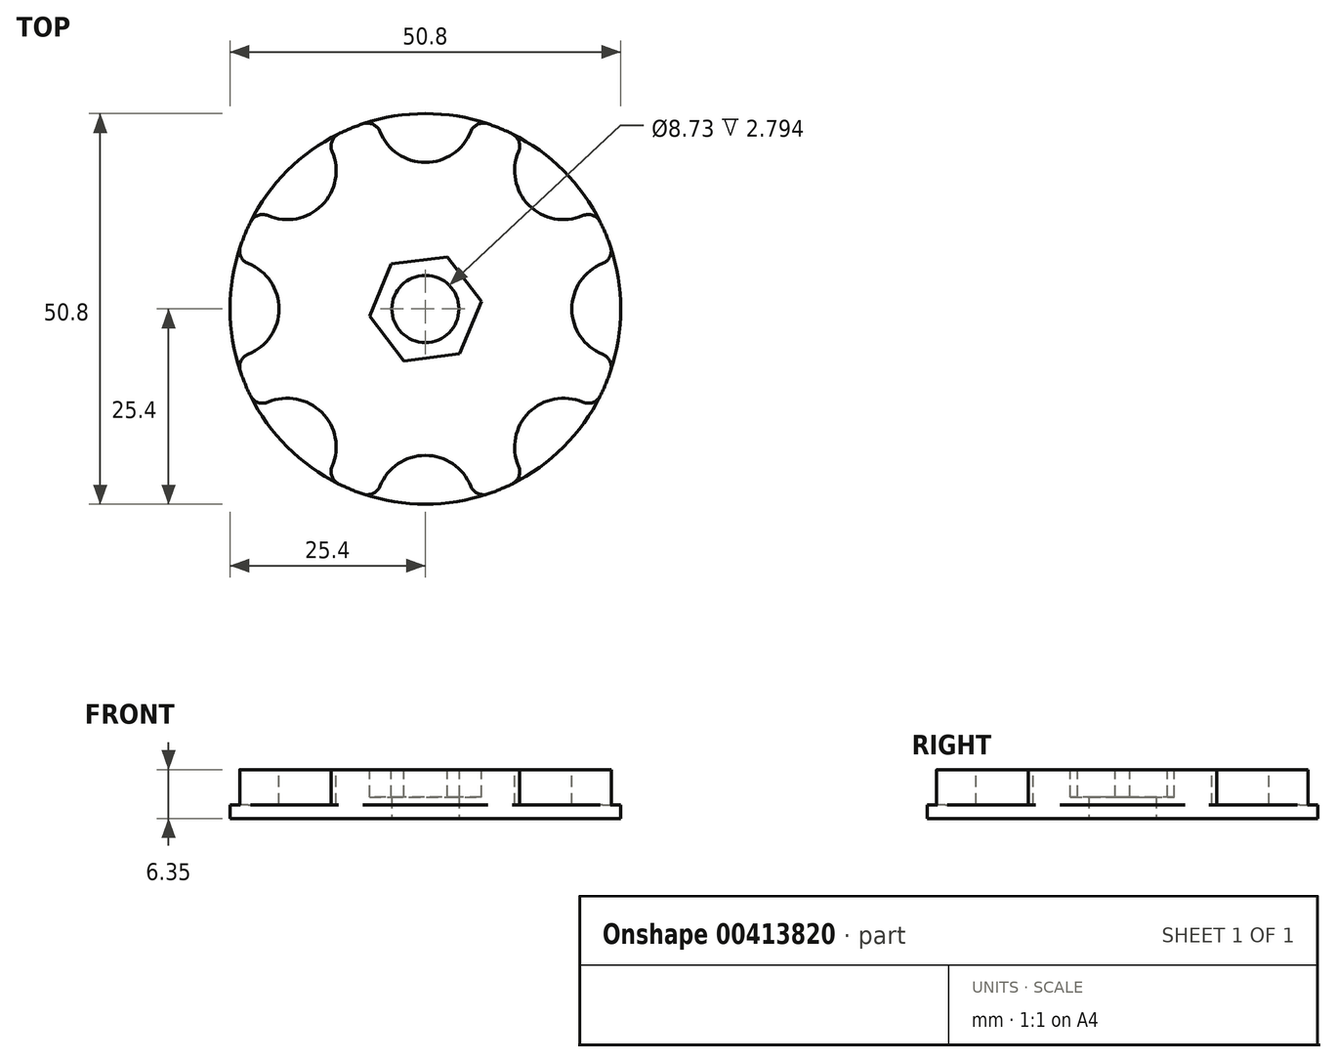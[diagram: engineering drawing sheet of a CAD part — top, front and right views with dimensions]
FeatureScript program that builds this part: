
annotation { "Feature Type Name" : "Feature", "Feature Type Description" : "" }
export const myFeature = defineFeature(function(context is Context, id is Id, definition is map)
    precondition{}
    {
        {
            var Q0;
            Q0=qCreatedBy(makeId("Top.planeOp"),FACE);
            var sketch = newSketch(context, id + "F0", { "sketchPlane" : qUnion([Q0])});
            skCircle(sketch, "E0", {"center": v(0, 0) * mm, "radius": 4.37 * mm});
            skCircle(sketch, "E1", {"center": v(0, 0) * mm, "radius": 25.4 * mm});
            skSolve(sketch);
        }
        {
            var Q0;
            Q0=makeQuery(id+"F0.imprint","IMPRINT",FACE,{"disambiguationData":[TD([[makeQuery(id+"F0.imprint","IMPRINT",EDGE,{"derivedFrom":sQuery(id+"F0.wireOp",EDGE,"E0")}),-1.0]])]});
            extrude(context, id + "F1", {"entities" : qUnion([Q0]), "depth" : 6.35 * mm});
        }
        {
            var Q0;
            Q0=makeQuery(id+"F1.opExtrude","CAP_FACE",FACE,{"disambiguationData":[OSD([sQuery(id+"F0.wireOp",EDGE,"E0"),sQuery(id+"F0.wireOp",EDGE,"E1")])],"isStart":false});
            var sketch = newSketch(context, id + "F2", { "sketchPlane" : qUnion([Q0])});
            skCircle(sketch, "E2.cCircle", {"center": v(0, 0) * mm, "radius": 6.35 * mm, "construction": true});
            skLineSegment(sketch, "E2.0", {"start": v(-2.82, -6.77) * mm, "end": v(-7.27, -0.94) * mm});
            skLineSegment(sketch, "E2.1", {"start": v(-7.27, -0.94) * mm, "end": v(-4.45, 5.83) * mm});
            skLineSegment(sketch, "E2.2", {"start": v(-4.45, 5.83) * mm, "end": v(2.82, 6.77) * mm});
            skLineSegment(sketch, "E2.3", {"start": v(2.82, 6.77) * mm, "end": v(7.27, 0.94) * mm});
            skLineSegment(sketch, "E2.4", {"start": v(7.27, 0.94) * mm, "end": v(4.45, -5.83) * mm});
            skLineSegment(sketch, "E2.5", {"start": v(4.45, -5.83) * mm, "end": v(-2.82, -6.77) * mm});
            skPoint(sketch, "E2.0.midPoint", {"position": v(-5.05, -3.85) * mm});
            skSolve(sketch);
        }
        {
            var Q0;
            Q0=makeQuery(id+"F2.imprint","IMPRINT",FACE,{"disambiguationData":[TD([[makeQuery(id+"F2.imprint","IMPRINT",EDGE,{"derivedFrom":sQuery(id+"F2.wireOp",EDGE,"E2.0")}),-1.0]])]});
            extrude(context, id + "F3", {"entities" : qUnion([Q0]), "operationType" : NewBodyOperationType.REMOVE, "oppositeDirection" : true, "depth" : 3.56 * mm});
        }
        {
            var Q0;
            Q0=makeQuery(id+"F1.opExtrude","CAP_FACE",FACE,{"disambiguationData":[OSD([sQuery(id+"F0.wireOp",EDGE,"E0"),sQuery(id+"F0.wireOp",EDGE,"E1")])],"isStart":false});
            var sketch = newSketch(context, id + "F4", { "sketchPlane" : qUnion([Q0])});
            skCircle(sketch, "E3", {"center": v(0, 25.4) * mm, "radius": 6.35 * mm});
            skCircle(sketch, "E4.1.0", {"center": v(-17.96, 17.96) * mm, "radius": 6.35 * mm});
            skCircle(sketch, "E4.2.0", {"center": v(-25.4, 0) * mm, "radius": 6.35 * mm});
            skCircle(sketch, "E4.3.0", {"center": v(-17.96, -17.96) * mm, "radius": 6.35 * mm});
            skCircle(sketch, "E4.4.0", {"center": v(0, -25.4) * mm, "radius": 6.35 * mm});
            skCircle(sketch, "E4.5.0", {"center": v(17.96, -17.96) * mm, "radius": 6.35 * mm});
            skCircle(sketch, "E4.6.0", {"center": v(25.4, 0) * mm, "radius": 6.35 * mm});
            skCircle(sketch, "E4.7.0", {"center": v(17.96, 17.96) * mm, "radius": 6.35 * mm});
            skPoint(sketch, "E4.center", {"position": v(0, 0) * mm});
            skSolve(sketch);
        }
        {
            var Q0;
            Q0 = qSketchRegion(id + "F4", true);
            extrude(context, id + "F5", {"entities" : qUnion([Q0]), "operationType" : NewBodyOperationType.REMOVE, "oppositeDirection" : true, "depth" : 4.57 * mm});
        }
        {
            var Q0;
            Q0=makeQuery(id+"F5.boolean.opBoolean","INTERSECT",EDGE,{"disambiguationData":[OD(0.0)],"derivedFrom":[makeQuery(id+"F1.opExtrude","SWEPT_FACE",FACE,{"disambiguationData":[OSD([sQuery(id+"F0.wireOp",EDGE,"E1")])]}),makeQuery(id+"F5.opExtrude","SWEPT_FACE",FACE,{"disambiguationData":[OSD([sQuery(id+"F4.wireOp",EDGE,"E4.5.0")])]})]});
            var Q1;
            Q1=makeQuery(id+"F5.boolean.opBoolean","INTERSECT",EDGE,{"disambiguationData":[OD(1.0)],"derivedFrom":[makeQuery(id+"F1.opExtrude","SWEPT_FACE",FACE,{"disambiguationData":[OSD([sQuery(id+"F0.wireOp",EDGE,"E1")])]}),makeQuery(id+"F5.opExtrude","SWEPT_FACE",FACE,{"disambiguationData":[OSD([sQuery(id+"F4.wireOp",EDGE,"E4.5.0")])]})]});
            var Q2;
            Q2=makeQuery(id+"F5.boolean.opBoolean","INTERSECT",EDGE,{"disambiguationData":[OD(0.0)],"derivedFrom":[makeQuery(id+"F1.opExtrude","SWEPT_FACE",FACE,{"disambiguationData":[OSD([sQuery(id+"F0.wireOp",EDGE,"E1")])]}),makeQuery(id+"F5.opExtrude","SWEPT_FACE",FACE,{"disambiguationData":[OSD([sQuery(id+"F4.wireOp",EDGE,"E4.6.0")])]})]});
            var Q3;
            Q3=makeQuery(id+"F5.boolean.opBoolean","INTERSECT",EDGE,{"disambiguationData":[OD(1.0)],"derivedFrom":[makeQuery(id+"F1.opExtrude","SWEPT_FACE",FACE,{"disambiguationData":[OSD([sQuery(id+"F0.wireOp",EDGE,"E1")])]}),makeQuery(id+"F5.opExtrude","SWEPT_FACE",FACE,{"disambiguationData":[OSD([sQuery(id+"F4.wireOp",EDGE,"E4.6.0")])]})]});
            var Q4;
            Q4=makeQuery(id+"F5.boolean.opBoolean","INTERSECT",EDGE,{"disambiguationData":[OD(1.0)],"derivedFrom":[makeQuery(id+"F1.opExtrude","SWEPT_FACE",FACE,{"disambiguationData":[OSD([sQuery(id+"F0.wireOp",EDGE,"E1")])]}),makeQuery(id+"F5.opExtrude","SWEPT_FACE",FACE,{"disambiguationData":[OSD([sQuery(id+"F4.wireOp",EDGE,"E4.7.0")])]})]});
            var Q5;
            Q5=makeQuery(id+"F5.boolean.opBoolean","INTERSECT",EDGE,{"disambiguationData":[OD(0.0)],"derivedFrom":[makeQuery(id+"F1.opExtrude","SWEPT_FACE",FACE,{"disambiguationData":[OSD([sQuery(id+"F0.wireOp",EDGE,"E1")])]}),makeQuery(id+"F5.opExtrude","SWEPT_FACE",FACE,{"disambiguationData":[OSD([sQuery(id+"F4.wireOp",EDGE,"E4.7.0")])]})]});
            var Q6;
            Q6=makeQuery(id+"F5.boolean.opBoolean","INTERSECT",EDGE,{"disambiguationData":[OD(0.0)],"derivedFrom":[makeQuery(id+"F1.opExtrude","SWEPT_FACE",FACE,{"disambiguationData":[OSD([sQuery(id+"F0.wireOp",EDGE,"E1")])]}),makeQuery(id+"F5.opExtrude","SWEPT_FACE",FACE,{"disambiguationData":[OSD([sQuery(id+"F4.wireOp",EDGE,"E4.4.0")])]})]});
            var Q7;
            Q7=makeQuery(id+"F5.boolean.opBoolean","INTERSECT",EDGE,{"disambiguationData":[OD(1.0)],"derivedFrom":[makeQuery(id+"F1.opExtrude","SWEPT_FACE",FACE,{"disambiguationData":[OSD([sQuery(id+"F0.wireOp",EDGE,"E1")])]}),makeQuery(id+"F5.opExtrude","SWEPT_FACE",FACE,{"disambiguationData":[OSD([sQuery(id+"F4.wireOp",EDGE,"E3")])]})]});
            var Q8;
            Q8=makeQuery(id+"F5.boolean.opBoolean","INTERSECT",EDGE,{"disambiguationData":[OD(0.0)],"derivedFrom":[makeQuery(id+"F1.opExtrude","SWEPT_FACE",FACE,{"disambiguationData":[OSD([sQuery(id+"F0.wireOp",EDGE,"E1")])]}),makeQuery(id+"F5.opExtrude","SWEPT_FACE",FACE,{"disambiguationData":[OSD([sQuery(id+"F4.wireOp",EDGE,"E3")])]})]});
            var Q9;
            Q9=makeQuery(id+"F5.boolean.opBoolean","INTERSECT",EDGE,{"disambiguationData":[OD(1.0)],"derivedFrom":[makeQuery(id+"F1.opExtrude","SWEPT_FACE",FACE,{"disambiguationData":[OSD([sQuery(id+"F0.wireOp",EDGE,"E1")])]}),makeQuery(id+"F5.opExtrude","SWEPT_FACE",FACE,{"disambiguationData":[OSD([sQuery(id+"F4.wireOp",EDGE,"E4.1.0")])]})]});
            var Q10;
            Q10=makeQuery(id+"F5.boolean.opBoolean","INTERSECT",EDGE,{"disambiguationData":[OD(0.0)],"derivedFrom":[makeQuery(id+"F1.opExtrude","SWEPT_FACE",FACE,{"disambiguationData":[OSD([sQuery(id+"F0.wireOp",EDGE,"E1")])]}),makeQuery(id+"F5.opExtrude","SWEPT_FACE",FACE,{"disambiguationData":[OSD([sQuery(id+"F4.wireOp",EDGE,"E4.1.0")])]})]});
            var Q11;
            Q11=makeQuery(id+"F5.boolean.opBoolean","INTERSECT",EDGE,{"disambiguationData":[OD(1.0)],"derivedFrom":[makeQuery(id+"F1.opExtrude","SWEPT_FACE",FACE,{"disambiguationData":[OSD([sQuery(id+"F0.wireOp",EDGE,"E1")])]}),makeQuery(id+"F5.opExtrude","SWEPT_FACE",FACE,{"disambiguationData":[OSD([sQuery(id+"F4.wireOp",EDGE,"E4.2.0")])]})]});
            var Q12;
            Q12=makeQuery(id+"F5.boolean.opBoolean","INTERSECT",EDGE,{"disambiguationData":[OD(0.0)],"derivedFrom":[makeQuery(id+"F1.opExtrude","SWEPT_FACE",FACE,{"disambiguationData":[OSD([sQuery(id+"F0.wireOp",EDGE,"E1")])]}),makeQuery(id+"F5.opExtrude","SWEPT_FACE",FACE,{"disambiguationData":[OSD([sQuery(id+"F4.wireOp",EDGE,"E4.2.0")])]})]});
            var Q13;
            Q13=makeQuery(id+"F5.boolean.opBoolean","INTERSECT",EDGE,{"disambiguationData":[OD(1.0)],"derivedFrom":[makeQuery(id+"F1.opExtrude","SWEPT_FACE",FACE,{"disambiguationData":[OSD([sQuery(id+"F0.wireOp",EDGE,"E1")])]}),makeQuery(id+"F5.opExtrude","SWEPT_FACE",FACE,{"disambiguationData":[OSD([sQuery(id+"F4.wireOp",EDGE,"E4.4.0")])]})]});
            var Q14;
            Q14=makeQuery(id+"F5.boolean.opBoolean","INTERSECT",EDGE,{"disambiguationData":[OD(1.0)],"derivedFrom":[makeQuery(id+"F1.opExtrude","SWEPT_FACE",FACE,{"disambiguationData":[OSD([sQuery(id+"F0.wireOp",EDGE,"E1")])]}),makeQuery(id+"F5.opExtrude","SWEPT_FACE",FACE,{"disambiguationData":[OSD([sQuery(id+"F4.wireOp",EDGE,"E4.3.0")])]})]});
            var Q15;
            Q15=makeQuery(id+"F5.boolean.opBoolean","INTERSECT",EDGE,{"disambiguationData":[OD(0.0)],"derivedFrom":[makeQuery(id+"F1.opExtrude","SWEPT_FACE",FACE,{"disambiguationData":[OSD([sQuery(id+"F0.wireOp",EDGE,"E1")])]}),makeQuery(id+"F5.opExtrude","SWEPT_FACE",FACE,{"disambiguationData":[OSD([sQuery(id+"F4.wireOp",EDGE,"E4.3.0")])]})]});
            fillet(context, id + "F6", {"entities" : qUnion([Q0, Q1, Q2, Q3, Q4, Q5, Q6, Q7, Q8, Q9, Q10, Q11, Q12, Q13, Q14, Q15]), "radius" : 1.78 * mm, "tangentPropagation" : true, "allowEdgeOverflow" : false});
        }
    });
